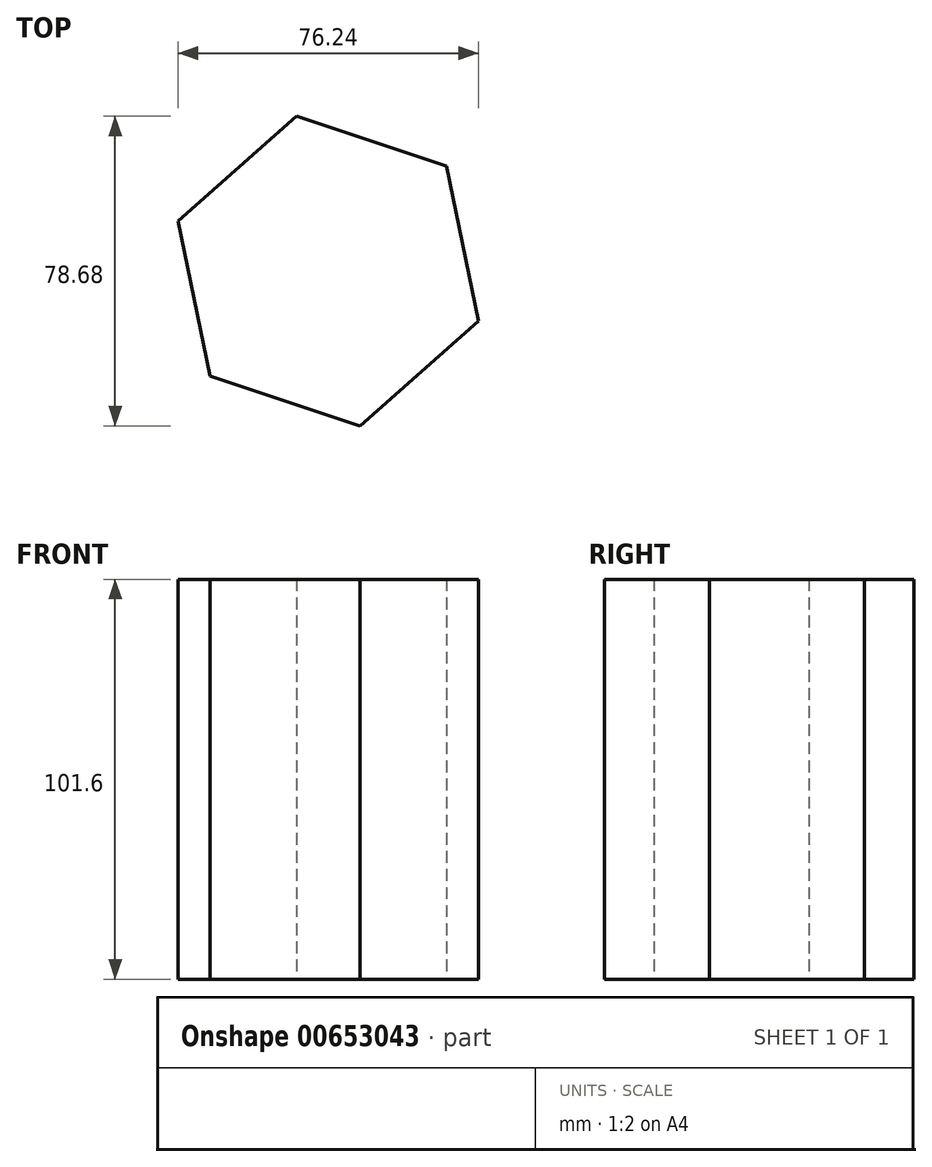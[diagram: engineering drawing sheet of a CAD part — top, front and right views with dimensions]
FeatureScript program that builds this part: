
annotation { "Feature Type Name" : "Feature", "Feature Type Description" : "" }
export const myFeature = defineFeature(function(context is Context, id is Id, definition is map)
    precondition{}
    {
        {
            var Q0;
            Q0=qCreatedBy(makeId("Top.planeOp"),FACE);
            var sketch = newSketch(context, id + "F0", { "sketchPlane" : qUnion([Q0])});
            skCircle(sketch, "E0.cCircle", {"center": v(0, 0) * mm, "radius": 40.17 * mm, "construction": true});
            skLineSegment(sketch, "E0.0", {"start": v(-8.1, 39.34) * mm, "end": v(30.02, 26.7) * mm});
            skLineSegment(sketch, "E0.1", {"start": v(30.02, 26.7) * mm, "end": v(38.12, -12.65) * mm});
            skLineSegment(sketch, "E0.2", {"start": v(38.12, -12.65) * mm, "end": v(8.1, -39.34) * mm});
            skLineSegment(sketch, "E0.3", {"start": v(8.1, -39.34) * mm, "end": v(-30.02, -26.7) * mm});
            skLineSegment(sketch, "E0.4", {"start": v(-30.02, -26.7) * mm, "end": v(-38.12, 12.65) * mm});
            skLineSegment(sketch, "E0.5", {"start": v(-38.12, 12.65) * mm, "end": v(-8.1, 39.34) * mm});
            skSolve(sketch);
        }
        {
            var Q0;
            Q0=makeQuery(id+"F0.imprint","IMPRINT",FACE,{"disambiguationData":[TD([[makeQuery(id+"F0.imprint","IMPRINT",EDGE,{"derivedFrom":sQuery(id+"F0.wireOp",EDGE,"E0.0")}),-1.0]])]});
            extrude(context, id + "F1", {"entities" : qUnion([Q0]), "depth" : 50.8 * mm, "offsetDistance" : 25.4 * mm, "hasSecondDirection" : true, "secondDirectionOppositeDirection" : true, "secondDirectionDepth" : 50.8 * mm});
        }
    });
